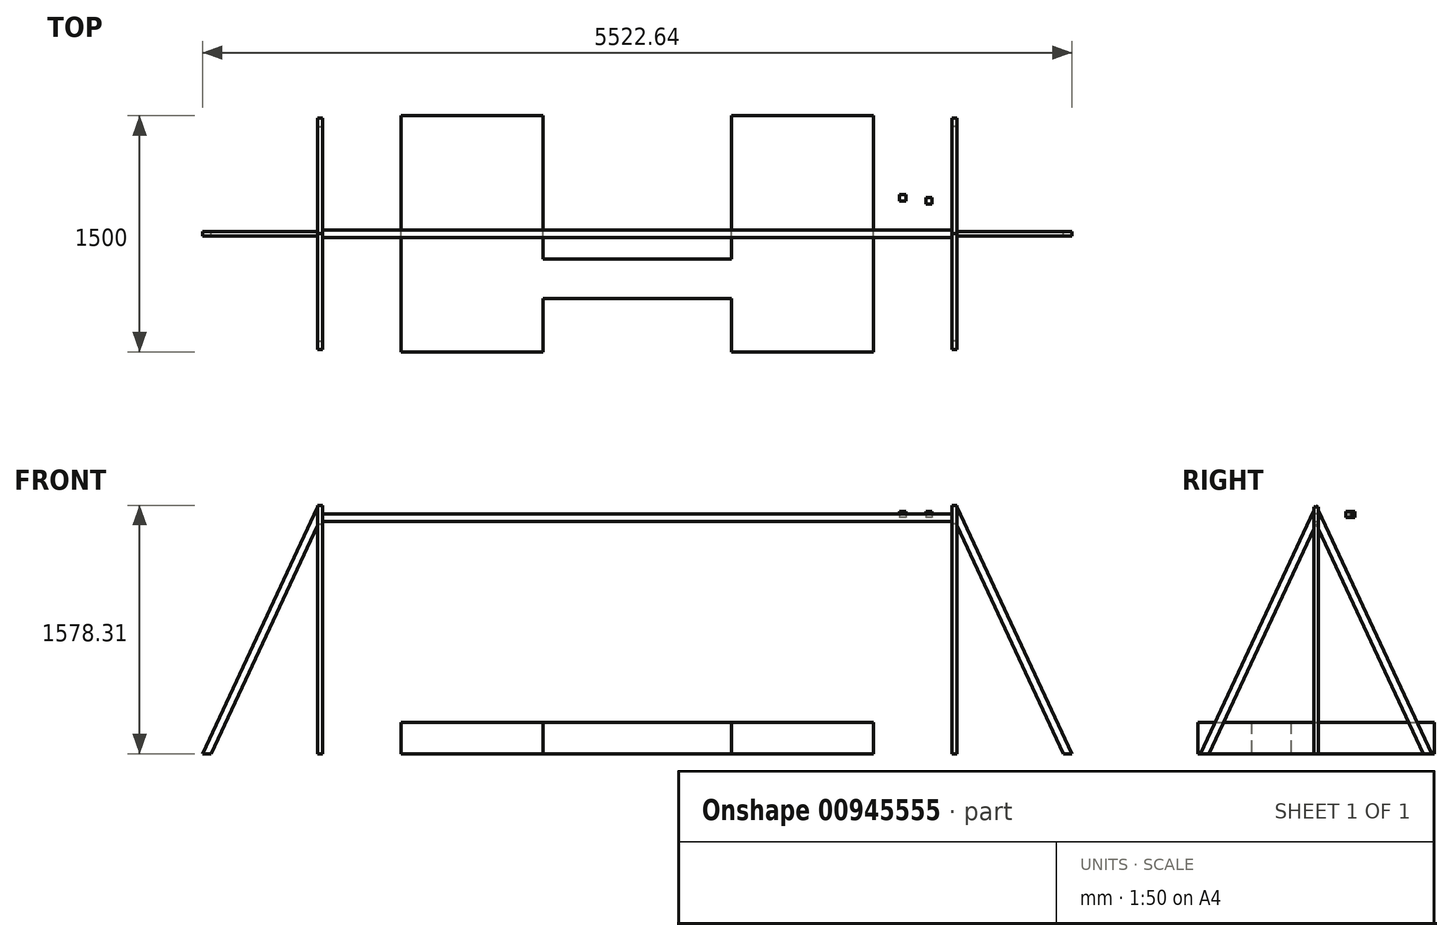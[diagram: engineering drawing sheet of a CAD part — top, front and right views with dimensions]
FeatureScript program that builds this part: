
annotation { "Feature Type Name" : "Feature", "Feature Type Description" : "" }
export const myFeature = defineFeature(function(context is Context, id is Id, definition is map)
    precondition{}
    {
        {
            var Q0;
            Q0=qCreatedBy(makeId("Right.planeOp"),FACE);
            var sketch = newSketch(context, id + "F0", { "sketchPlane" : qUnion([Q0])});
            skCircle(sketch, "E0", {"center": v(0, 0) * mm, "radius": 25 * mm});
            skSolve(sketch);
        }
        {
            var Q0;
            Q0=makeQuery(id+"F0.imprint","IMPRINT",FACE,{"disambiguationData":[TD([[makeQuery(id+"F0.imprint","IMPRINT",EDGE,{"derivedFrom":sQuery(id+"F0.wireOp",EDGE,"E0")}),1.0]])]});
            extrude(context, id + "F1", {"entities" : qUnion([Q0]), "oppositeDirection" : true, "depth" : 2000 * mm, "offsetDistance" : 25 * mm});
        }
        {
            var Q0;
            Q0=makeQuery(id+"F1.opExtrude","CAP_FACE",FACE,{"disambiguationData":[OSD([sQuery(id+"F0.wireOp",EDGE,"E0")])],"isStart":true});
            var sketch = newSketch(context, id + "F2", { "sketchPlane" : qUnion([Q0])});
            skLineSegment(sketch, "E1", {"start": v(0, -40) * mm, "end": v(0, 78.31) * mm});
            skLineSegment(sketch, "E2", {"start": v(0, 78.31) * mm, "end": v(-735.98, -1500) * mm});
            skLineSegment(sketch, "E3", {"start": v(-735.98, -1500) * mm, "end": v(-680.8, -1500) * mm});
            skLineSegment(sketch, "E4", {"start": v(-680.8, -1500) * mm, "end": v(0, -40) * mm});
            skLineSegment(sketch, "E5.MirrorCS", {"start": v(0, 78.31) * mm, "end": v(735.98, -1500) * mm});
            skLineSegment(sketch, "E6.MirrorCS", {"start": v(680.8, -1500) * mm, "end": v(0, -40) * mm});
            skLineSegment(sketch, "E7.MirrorCS", {"start": v(735.98, -1500) * mm, "end": v(680.8, -1500) * mm});
            skSolve(sketch);
        }
        {
            var Q0;
            Q0 = qSketchRegion(id + "F2", true);
            extrude(context, id + "F3", {"entities" : qUnion([Q0]), "operationType" : NewBodyOperationType.ADD, "depth" : 30 * mm, "offsetDistance" : 25 * mm});
        }
        {
            var Q0;
            Q0=qCreatedBy(makeId("Front.planeOp"),FACE);
            var sketch = newSketch(context, id + "F4", { "sketchPlane" : qUnion([Q0])});
            skLineSegment(sketch, "E8", {"start": v(30, 68.31) * mm, "end": v(761.32, -1500) * mm});
            skLineSegment(sketch, "E9", {"start": v(761.32, -1500) * mm, "end": v(706.15, -1500) * mm});
            skLineSegment(sketch, "E10", {"start": v(706.15, -1500) * mm, "end": v(30, -50) * mm});
            skLineSegment(sketch, "E11", {"start": v(30, -50) * mm, "end": v(30, 68.31) * mm});
            skSolve(sketch);
        }
        {
            var Q0;
            Q0 = qSketchRegion(id + "F4", true);
            extrude(context, id + "F5", {"entities" : qUnion([Q0]), "operationType" : NewBodyOperationType.ADD, "endBound" : BoundingType.SYMMETRIC, "depth" : 30 * mm, "offsetDistance" : 25 * mm});
        }
        {
            var Q0;
            Q0=makeQuery(id+"F3.opExtrude","SWEPT_FACE",FACE,{"disambiguationData":[OSD([sQuery(id+"F2.wireOp",EDGE,"E7.MirrorCS")])]});
            var sketch = newSketch(context, id + "F6", { "sketchPlane" : qUnion([Q0])});
            skLineSegment(sketch, "E12.bottom", {"start": v(-500, 750) * mm, "end": v(-1400, 750) * mm});
            skLineSegment(sketch, "E12.top", {"start": v(-500, -750) * mm, "end": v(-1400, -750) * mm});
            skLineSegment(sketch, "E12.left", {"start": v(-500, 750) * mm, "end": v(-500, -750) * mm});
            skLineSegment(sketch, "E12.right", {"start": v(-1400, 750) * mm, "end": v(-1400, -750) * mm});
            skLineSegment(sketch, "E13.bottom", {"start": v(-1400, 410) * mm, "end": v(-2000, 410) * mm});
            skLineSegment(sketch, "E13.top", {"start": v(-1400, 160) * mm, "end": v(-2000, 160) * mm});
            skLineSegment(sketch, "E13.left", {"start": v(-1400, 410) * mm, "end": v(-1400, 160) * mm});
            skLineSegment(sketch, "E13.right", {"start": v(-2000, 410) * mm, "end": v(-2000, 160) * mm});
            skSolve(sketch);
        }
        {
            var Q0;
            Q0 = qSketchRegion(id + "F6", true);
            extrude(context, id + "F7", {"entities" : qUnion([Q0]), "oppositeDirection" : true, "depth" : 200 * mm, "offsetDistance" : 25 * mm});
        }
        {
            var Q0;
            Q0=makeQuery(id+"F1.opExtrude","SWEPT_BODY",BODY,{"disambiguationData":[OSD([sQuery(id+"F0.wireOp",EDGE,"E0")])]});
            var Q1;
            Q1=makeQuery(id+"F7.opExtrude","SWEPT_BODY",BODY,{"disambiguationData":[OSD([sQuery(id+"F6.wireOp",EDGE,"E12.bottom"),sQuery(id+"F6.wireOp",EDGE,"E12.top"),sQuery(id+"F6.wireOp",EDGE,"E12.left"),sQuery(id+"F6.wireOp",EDGE,"E12.right"),sQuery(id+"F6.wireOp",EDGE,"E13.bottom"),sQuery(id+"F6.wireOp",EDGE,"E13.top"),sQuery(id+"F6.wireOp",EDGE,"E13.right")])]});
            var Q2;
            Q2=makeQuery(id+"F1.opExtrude","CAP_FACE",FACE,{"disambiguationData":[OSD([sQuery(id+"F0.wireOp",EDGE,"E0")])],"isStart":false});
            mirror(context, id + "F8", {"operationType" : NewBodyOperationType.ADD, "entities" : qUnion([Q0, Q1]), "mirrorPlane" : qUnion([Q2])});
        }
        {
            var Q0;
            Q0=qCreatedBy(makeId("Top.planeOp"),FACE);
            var sketch = newSketch(context, id + "F9", { "sketchPlane" : qUnion([Q0])});
            skLineSegment(sketch, "E14.bottom", {"start": v(-127.1, 228.85) * mm, "end": v(-167.1, 228.85) * mm});
            skLineSegment(sketch, "E14.top", {"start": v(-127.1, 188.85) * mm, "end": v(-167.1, 188.85) * mm});
            skLineSegment(sketch, "E14.left", {"start": v(-127.1, 228.85) * mm, "end": v(-127.1, 188.85) * mm});
            skLineSegment(sketch, "E14.right", {"start": v(-167.1, 228.85) * mm, "end": v(-167.1, 188.85) * mm});
            skSolve(sketch);
        }
        {
            var Q0;
            Q0=makeQuery(id+"F9.imprint","IMPRINT",FACE,{"disambiguationData":[TD([[makeQuery(id+"F9.imprint","IMPRINT",EDGE,{"derivedFrom":sQuery(id+"F9.wireOp",EDGE,"E14.bottom")}),1.0]])]});
            extrude(context, id + "F10", {"entities" : qUnion([Q0]), "depth" : 40 * mm, "offsetDistance" : 25 * mm});
        }
        {
            var Q0;
            Q0=qCreatedBy(makeId("Top.planeOp"),FACE);
            var sketch = newSketch(context, id + "F11", { "sketchPlane" : qUnion([Q0])});
            skLineSegment(sketch, "E15.bottom", {"start": v(-293.92, 247.87) * mm, "end": v(-333.92, 247.87) * mm});
            skLineSegment(sketch, "E15.top", {"start": v(-293.92, 207.87) * mm, "end": v(-333.92, 207.87) * mm});
            skLineSegment(sketch, "E15.left", {"start": v(-293.92, 247.87) * mm, "end": v(-293.92, 207.87) * mm});
            skLineSegment(sketch, "E15.right", {"start": v(-333.92, 247.87) * mm, "end": v(-333.92, 207.87) * mm});
            skSolve(sketch);
        }
        {
            var Q0;
            Q0 = qSketchRegion(id + "F11", true);
            extrude(context, id + "F12", {"entities" : qUnion([Q0]), "depth" : 40 * mm, "offsetDistance" : 25 * mm});
        }
    });
